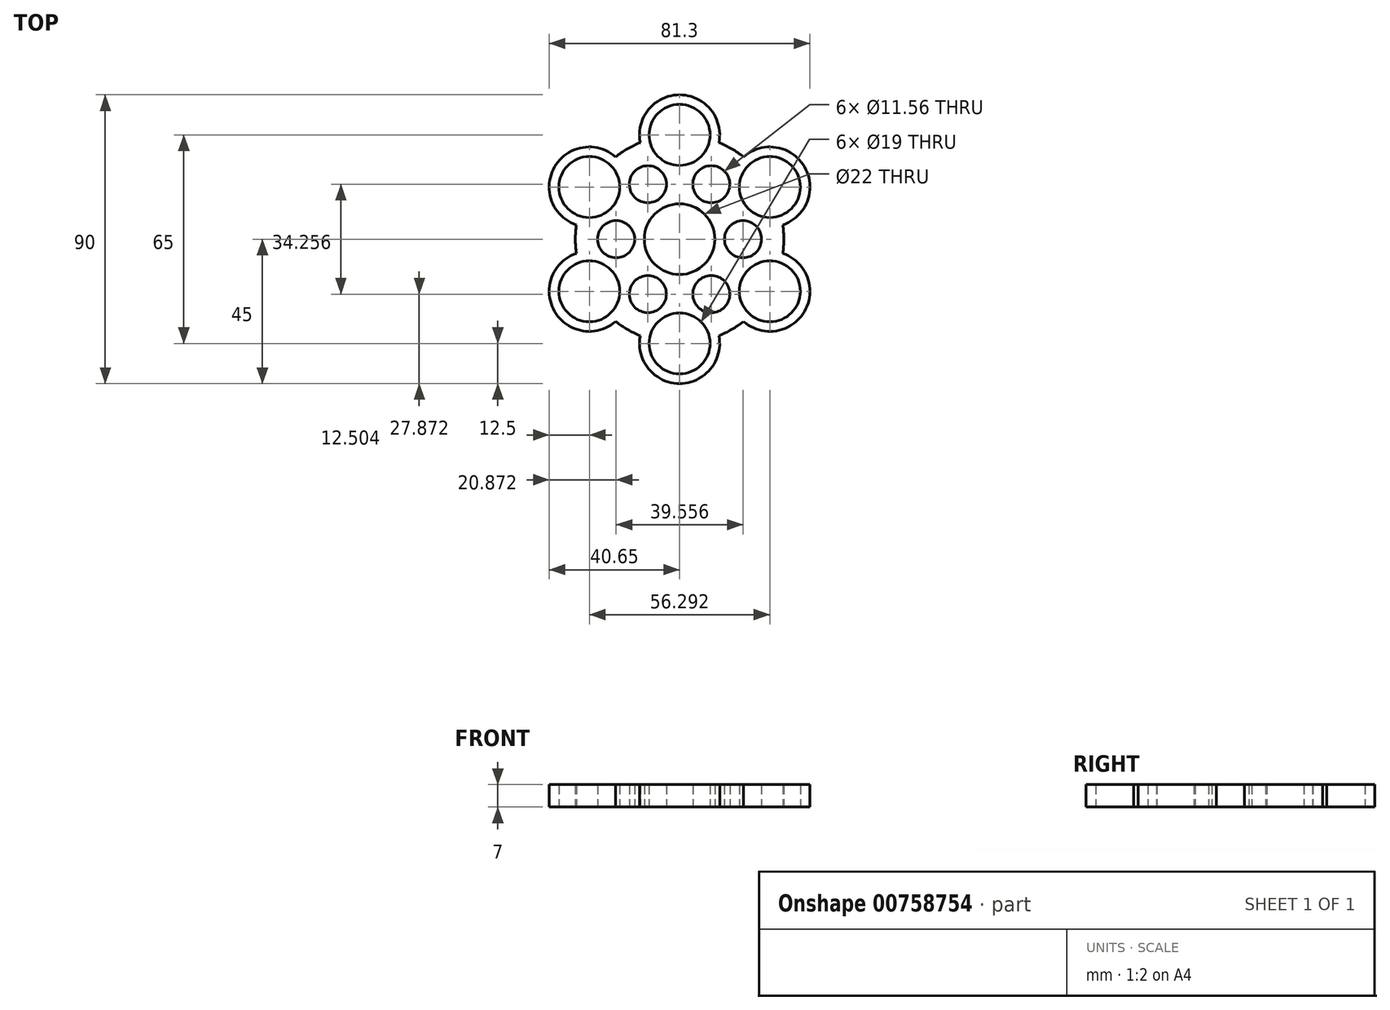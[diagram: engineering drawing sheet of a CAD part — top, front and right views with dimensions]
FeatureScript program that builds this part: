
annotation { "Feature Type Name" : "Feature", "Feature Type Description" : "" }
export const myFeature = defineFeature(function(context is Context, id is Id, definition is map)
    precondition{}
    {
        {
            var Q0;
            Q0=qCreatedBy(makeId("Top.planeOp"),FACE);
            var sketch = newSketch(context, id + "F0", { "sketchPlane" : qUnion([Q0])});
            skCircle(sketch, "E0", {"center": v(0, 0) * mm, "radius": 11 * mm});
            skCircle(sketch, "E1", {"center": v(0, 0) * mm, "radius": 14 * mm});
            skCircle(sketch, "E2", {"center": v(0, 32.5) * mm, "radius": 9.5 * mm});
            skArc(sketch, "E3.trimOffspring", {"start": v(12.27, 30.1) * mm, "mid": v(0, 45) * mm, "end": v(-12.27, 30.1) * mm});
            skCircle(sketch, "E4", {"center": v(0, 32.5) * mm, "radius": 12.5 * mm});
            skArc(sketch, "E5", {"start": v(-28.71, 6.77) * mm, "mid": v(-29.5, 0) * mm, "end": v(-28.71, -6.77) * mm});
            skArc(sketch, "E6", {"start": v(-31.64, 7.42) * mm, "mid": v(-32.5, 0) * mm, "end": v(-31.64, -7.42) * mm});
            skCircle(sketch, "E7.1.0", {"center": v(-28.15, 16.25) * mm, "radius": 12.5 * mm});
            skCircle(sketch, "E7.1.1", {"center": v(-28.15, 16.25) * mm, "radius": 9.5 * mm});
            skCircle(sketch, "E7.2.0", {"center": v(-28.15, -16.25) * mm, "radius": 12.5 * mm});
            skCircle(sketch, "E7.2.1", {"center": v(-28.15, -16.25) * mm, "radius": 9.5 * mm});
            skCircle(sketch, "E8.1.3.0", {"center": v(0, -32.5) * mm, "radius": 12.5 * mm});
            skCircle(sketch, "E8.2.3.0", {"center": v(0, -32.5) * mm, "radius": 9.5 * mm});
            skCircle(sketch, "E8.1.4.0", {"center": v(28.15, -16.25) * mm, "radius": 12.5 * mm});
            skCircle(sketch, "E8.2.4.0", {"center": v(28.15, -16.25) * mm, "radius": 9.5 * mm});
            skCircle(sketch, "E8.1.5.0", {"center": v(28.15, 16.25) * mm, "radius": 12.5 * mm});
            skCircle(sketch, "E8.2.5.0", {"center": v(28.15, 16.25) * mm, "radius": 9.5 * mm});
            skArc(sketch, "E9.trimOffspring", {"start": v(-9.4, 31.11) * mm, "mid": v(-16.25, 28.15) * mm, "end": v(-22.24, 23.7) * mm});
            skArc(sketch, "E10.trimOffspring", {"start": v(-8.5, 28.25) * mm, "mid": v(-14.75, 25.55) * mm, "end": v(-20.22, 21.48) * mm});
            skArc(sketch, "E11.trimOffspring", {"start": v(20.22, 21.48) * mm, "mid": v(14.75, 25.55) * mm, "end": v(8.5, 28.25) * mm});
            skArc(sketch, "E12.trimOffspring", {"start": v(22.24, 23.7) * mm, "mid": v(16.25, 28.15) * mm, "end": v(9.4, 31.11) * mm});
            skArc(sketch, "E13.trimOffspring", {"start": v(31.64, -7.42) * mm, "mid": v(32.5, 0) * mm, "end": v(31.64, 7.42) * mm});
            skArc(sketch, "E14.trimOffspring", {"start": v(28.71, -6.77) * mm, "mid": v(29.5, 0) * mm, "end": v(28.71, 6.77) * mm});
            skArc(sketch, "E15.trimOffspring", {"start": v(9.4, -31.11) * mm, "mid": v(16.25, -28.15) * mm, "end": v(22.24, -23.7) * mm});
            skArc(sketch, "E16.trimOffspring", {"start": v(8.5, -28.25) * mm, "mid": v(14.75, -25.55) * mm, "end": v(20.22, -21.48) * mm});
            skArc(sketch, "E17.trimOffspring", {"start": v(-22.24, -23.7) * mm, "mid": v(-16.25, -28.15) * mm, "end": v(-9.4, -31.11) * mm});
            skArc(sketch, "E18.trimOffspring", {"start": v(-20.22, -21.48) * mm, "mid": v(-14.75, -25.55) * mm, "end": v(-8.5, -28.25) * mm});
            skCircle(sketch, "E19", {"center": v(-9.89, 17.12) * mm, "radius": 5.78 * mm});
            skPoint(sketch, "E19.first.point", {"position": v(-15.66, 16.85) * mm});
            skPoint(sketch, "E19.second.point", {"position": v(-6.76, 21.99) * mm});
            skPoint(sketch, "E19.third.point", {"position": v(-6.76, 12.26) * mm});
            skCircle(sketch, "E20", {"center": v(9.89, 17.13) * mm, "radius": 5.78 * mm});
            skPoint(sketch, "E20.first.point", {"position": v(6.76, 21.99) * mm});
            skPoint(sketch, "E20.second.point", {"position": v(7, 12.12) * mm});
            skPoint(sketch, "E20.third.point", {"position": v(15.66, 16.85) * mm});
            skCircle(sketch, "E21", {"center": v(19.78, 0) * mm, "radius": 5.78 * mm});
            skPoint(sketch, "E21.first.point", {"position": v(22.42, -5.14) * mm});
            skPoint(sketch, "E21.second.point", {"position": v(22.42, 5.14) * mm});
            skPoint(sketch, "E21.third.point", {"position": v(14, 0) * mm});
            skCircle(sketch, "E22", {"center": v(9.89, -17.13) * mm, "radius": 5.78 * mm});
            skPoint(sketch, "E22.first.point", {"position": v(6.76, -21.99) * mm});
            skPoint(sketch, "E22.second.point", {"position": v(15.66, -16.85) * mm});
            skPoint(sketch, "E22.third.point", {"position": v(7, -12.12) * mm});
            skCircle(sketch, "E23", {"center": v(-9.89, -17.13) * mm, "radius": 5.78 * mm});
            skPoint(sketch, "E23.first.point", {"position": v(-6.76, -21.99) * mm});
            skPoint(sketch, "E23.second.point", {"position": v(-15.66, -16.85) * mm});
            skPoint(sketch, "E23.third.point", {"position": v(-7, -12.12) * mm});
            skCircle(sketch, "E24", {"center": v(-19.78, 0) * mm, "radius": 5.78 * mm});
            skPoint(sketch, "E24.first.point", {"position": v(-22.42, -5.14) * mm});
            skPoint(sketch, "E24.second.point", {"position": v(-22.42, 5.14) * mm});
            skPoint(sketch, "E24.third.point", {"position": v(-14, 0) * mm});
            skSolve(sketch);
        }
        {
            var Q0;
            {var subQ0=sQuery(id+"F0.wireOp",EDGE,"E11.trimOffspring");var subQ1=sQuery(id+"F0.wireOp",EDGE,"E2");var subQ2=makeQuery(id+"F0.imprint","INTERSECT",VERTEX,{"derivedFrom":[subQ1,subQ0]});Q0=makeQuery(id+"F0.imprint","IMPRINT",FACE,{"disambiguationData":[TD([[makeQuery(id+"F0.imprint","IMPRINT",EDGE,{"disambiguationData":[TD([[subQ2,-1.0]])],"derivedFrom":subQ1}),-1.0]])]});}
            var Q1;
            {var subQ0=sQuery(id+"F0.wireOp",EDGE,"E7.2.1");var subQ1=sQuery(id+"F0.wireOp",EDGE,"E5");var subQ2=makeQuery(id+"F0.imprint","INTERSECT",VERTEX,{"derivedFrom":[subQ1,subQ0]});Q1=makeQuery(id+"F0.imprint","IMPRINT",FACE,{"disambiguationData":[TD([[makeQuery(id+"F0.imprint","IMPRINT",EDGE,{"disambiguationData":[TD([[subQ2,1.0]])],"derivedFrom":subQ1}),-1.0]])]});}
            var Q2;
            {var subQ0=sQuery(id+"F0.wireOp",EDGE,"E15.trimOffspring");var subQ1=sQuery(id+"F0.wireOp",EDGE,"E8.1.4.0");var subQ2=makeQuery(id+"F0.imprint","INTERSECT",VERTEX,{"derivedFrom":[subQ1,subQ0]});Q2=makeQuery(id+"F0.imprint","IMPRINT",FACE,{"disambiguationData":[TD([[makeQuery(id+"F0.imprint","IMPRINT",EDGE,{"disambiguationData":[TD([[subQ2,1.0]])],"derivedFrom":subQ1}),1.0]])]});}
            var Q3;
            {var subQ0=sQuery(id+"F0.wireOp",EDGE,"E11.trimOffspring");var subQ1=sQuery(id+"F0.wireOp",EDGE,"E8.1.5.0");var subQ2=makeQuery(id+"F0.imprint","INTERSECT",VERTEX,{"derivedFrom":[subQ1,subQ0]});Q3=makeQuery(id+"F0.imprint","IMPRINT",FACE,{"disambiguationData":[TD([[makeQuery(id+"F0.imprint","IMPRINT",EDGE,{"disambiguationData":[TD([[subQ2,-1.0]])],"derivedFrom":subQ1}),1.0]])]});}
            var Q4;
            {var subQ0=sQuery(id+"F0.wireOp",EDGE,"E7.1.1");var subQ1=sQuery(id+"F0.wireOp",EDGE,"E5");var subQ2=makeQuery(id+"F0.imprint","INTERSECT",VERTEX,{"derivedFrom":[subQ1,subQ0]});Q4=makeQuery(id+"F0.imprint","IMPRINT",FACE,{"disambiguationData":[TD([[makeQuery(id+"F0.imprint","IMPRINT",EDGE,{"disambiguationData":[TD([[subQ2,-1.0]])],"derivedFrom":subQ1}),1.0]])]});}
            var Q5;
            {var subQ0=sQuery(id+"F0.wireOp",EDGE,"E17.trimOffspring");var subQ1=sQuery(id+"F0.wireOp",EDGE,"E7.2.0");var subQ2=makeQuery(id+"F0.imprint","INTERSECT",VERTEX,{"derivedFrom":[subQ1,subQ0]});Q5=makeQuery(id+"F0.imprint","IMPRINT",FACE,{"disambiguationData":[TD([[makeQuery(id+"F0.imprint","IMPRINT",EDGE,{"disambiguationData":[TD([[subQ2,-1.0]])],"derivedFrom":subQ1}),1.0]])]});}
            var Q6;
            {var subQ0=sQuery(id+"F0.wireOp",EDGE,"E13.trimOffspring");var subQ1=sQuery(id+"F0.wireOp",EDGE,"E8.1.5.0");var subQ2=makeQuery(id+"F0.imprint","INTERSECT",VERTEX,{"derivedFrom":[subQ1,subQ0]});Q6=makeQuery(id+"F0.imprint","IMPRINT",FACE,{"disambiguationData":[TD([[makeQuery(id+"F0.imprint","IMPRINT",EDGE,{"disambiguationData":[TD([[subQ2,1.0]])],"derivedFrom":subQ1}),1.0]])]});}
            var Q7;
            {var subQ0=sQuery(id+"F0.wireOp",EDGE,"E9.trimOffspring");var subQ1=sQuery(id+"F0.wireOp",EDGE,"E2");var subQ2=makeQuery(id+"F0.imprint","INTERSECT",VERTEX,{"derivedFrom":[subQ1,subQ0]});Q7=makeQuery(id+"F0.imprint","IMPRINT",FACE,{"disambiguationData":[TD([[makeQuery(id+"F0.imprint","IMPRINT",EDGE,{"disambiguationData":[TD([[subQ2,1.0]])],"derivedFrom":subQ1}),-1.0]])]});}
            var Q8;
            {var subQ0=sQuery(id+"F0.wireOp",EDGE,"E10.trimOffspring");var subQ1=sQuery(id+"F0.wireOp",EDGE,"E2");var subQ2=makeQuery(id+"F0.imprint","INTERSECT",VERTEX,{"derivedFrom":[subQ1,subQ0]});Q8=makeQuery(id+"F0.imprint","IMPRINT",FACE,{"disambiguationData":[TD([[makeQuery(id+"F0.imprint","IMPRINT",EDGE,{"disambiguationData":[TD([[subQ2,-1.0]])],"derivedFrom":subQ1}),-1.0]])]});}
            var Q9;
            {var subQ0=sQuery(id+"F0.wireOp",EDGE,"E15.trimOffspring");var subQ1=sQuery(id+"F0.wireOp",EDGE,"E8.1.3.0");var subQ2=makeQuery(id+"F0.imprint","INTERSECT",VERTEX,{"derivedFrom":[subQ1,subQ0]});Q9=makeQuery(id+"F0.imprint","IMPRINT",FACE,{"disambiguationData":[TD([[makeQuery(id+"F0.imprint","IMPRINT",EDGE,{"disambiguationData":[TD([[subQ2,-1.0]])],"derivedFrom":subQ1}),-1.0]])]});}
            var Q10;
            {var subQ0=sQuery(id+"F0.wireOp",EDGE,"E7.2.1");var subQ1=sQuery(id+"F0.wireOp",EDGE,"E5");var subQ2=makeQuery(id+"F0.imprint","INTERSECT",VERTEX,{"derivedFrom":[subQ1,subQ0]});Q10=makeQuery(id+"F0.imprint","IMPRINT",FACE,{"disambiguationData":[TD([[makeQuery(id+"F0.imprint","IMPRINT",EDGE,{"disambiguationData":[TD([[subQ2,1.0]])],"derivedFrom":subQ1}),1.0]])]});}
            var Q11;
            {var subQ0=sQuery(id+"F0.wireOp",EDGE,"E12.trimOffspring");var subQ1=sQuery(id+"F0.wireOp",EDGE,"E8.1.5.0");var subQ2=makeQuery(id+"F0.imprint","INTERSECT",VERTEX,{"derivedFrom":[subQ1,subQ0]});Q11=makeQuery(id+"F0.imprint","IMPRINT",FACE,{"disambiguationData":[TD([[makeQuery(id+"F0.imprint","IMPRINT",EDGE,{"disambiguationData":[TD([[subQ2,1.0]])],"derivedFrom":subQ1}),1.0]])]});}
            var Q12;
            {var subQ0=sQuery(id+"F0.wireOp",EDGE,"E12.trimOffspring");var subQ1=sQuery(id+"F0.wireOp",EDGE,"E4");var subQ2=makeQuery(id+"F0.imprint","INTERSECT",VERTEX,{"derivedFrom":[subQ1,subQ0]});Q12=makeQuery(id+"F0.imprint","IMPRINT",FACE,{"disambiguationData":[TD([[makeQuery(id+"F0.imprint","IMPRINT",EDGE,{"disambiguationData":[TD([[subQ2,1.0]])],"derivedFrom":subQ1}),-1.0]])]});}
            var Q13;
            {var subQ0=sQuery(id+"F0.wireOp",EDGE,"E13.trimOffspring");var subQ1=sQuery(id+"F0.wireOp",EDGE,"E8.1.4.0");var subQ2=makeQuery(id+"F0.imprint","INTERSECT",VERTEX,{"derivedFrom":[subQ1,subQ0]});Q13=makeQuery(id+"F0.imprint","IMPRINT",FACE,{"disambiguationData":[TD([[makeQuery(id+"F0.imprint","IMPRINT",EDGE,{"disambiguationData":[TD([[subQ2,-1.0]])],"derivedFrom":subQ1}),1.0]])]});}
            var Q14;
            {var subQ0=sQuery(id+"F0.wireOp",EDGE,"E9.trimOffspring");var subQ1=sQuery(id+"F0.wireOp",EDGE,"E7.1.0");var subQ2=makeQuery(id+"F0.imprint","INTERSECT",VERTEX,{"derivedFrom":[subQ1,subQ0]});Q14=makeQuery(id+"F0.imprint","IMPRINT",FACE,{"disambiguationData":[TD([[makeQuery(id+"F0.imprint","IMPRINT",EDGE,{"disambiguationData":[TD([[subQ2,1.0]])],"derivedFrom":subQ1}),1.0]])]});}
            var Q15;
            {var subQ0=sQuery(id+"F0.wireOp",EDGE,"E12.trimOffspring");var subQ1=sQuery(id+"F0.wireOp",EDGE,"E8.1.5.0");var subQ2=makeQuery(id+"F0.imprint","INTERSECT",VERTEX,{"derivedFrom":[subQ1,subQ0]});Q15=makeQuery(id+"F0.imprint","IMPRINT",FACE,{"disambiguationData":[TD([[makeQuery(id+"F0.imprint","IMPRINT",EDGE,{"disambiguationData":[TD([[subQ2,-1.0]])],"derivedFrom":subQ1}),1.0]])]});}
            var Q16;
            {var subQ0=sQuery(id+"F0.wireOp",EDGE,"E13.trimOffspring");var subQ1=sQuery(id+"F0.wireOp",EDGE,"E8.1.4.0");var subQ2=makeQuery(id+"F0.imprint","INTERSECT",VERTEX,{"derivedFrom":[subQ1,subQ0]});Q16=makeQuery(id+"F0.imprint","IMPRINT",FACE,{"disambiguationData":[TD([[makeQuery(id+"F0.imprint","IMPRINT",EDGE,{"disambiguationData":[TD([[subQ2,1.0]])],"derivedFrom":subQ1}),1.0]])]});}
            var Q17;
            {var subQ0=sQuery(id+"F0.wireOp",EDGE,"E7.1.1");var subQ1=sQuery(id+"F0.wireOp",EDGE,"E6");var subQ2=makeQuery(id+"F0.imprint","INTERSECT",VERTEX,{"derivedFrom":[subQ1,subQ0]});Q17=makeQuery(id+"F0.imprint","IMPRINT",FACE,{"disambiguationData":[TD([[makeQuery(id+"F0.imprint","IMPRINT",EDGE,{"disambiguationData":[TD([[subQ2,-1.0]])],"derivedFrom":subQ1}),-1.0]])]});}
            var Q18;
            {var subQ0=sQuery(id+"F0.wireOp",EDGE,"E17.trimOffspring");var subQ1=sQuery(id+"F0.wireOp",EDGE,"E7.2.0");var subQ2=makeQuery(id+"F0.imprint","INTERSECT",VERTEX,{"derivedFrom":[subQ1,subQ0]});Q18=makeQuery(id+"F0.imprint","IMPRINT",FACE,{"disambiguationData":[TD([[makeQuery(id+"F0.imprint","IMPRINT",EDGE,{"disambiguationData":[TD([[subQ2,-1.0]])],"derivedFrom":subQ1}),-1.0]])]});}
            var Q19;
            {var subQ0=sQuery(id+"F0.wireOp",EDGE,"E17.trimOffspring");var subQ1=sQuery(id+"F0.wireOp",EDGE,"E8.1.3.0");var subQ2=makeQuery(id+"F0.imprint","INTERSECT",VERTEX,{"derivedFrom":[subQ1,subQ0]});Q19=makeQuery(id+"F0.imprint","IMPRINT",FACE,{"disambiguationData":[TD([[makeQuery(id+"F0.imprint","IMPRINT",EDGE,{"disambiguationData":[TD([[subQ2,1.0]])],"derivedFrom":subQ1}),1.0]])]});}
            var Q20;
            {var subQ0=sQuery(id+"F0.wireOp",EDGE,"E15.trimOffspring");var subQ1=sQuery(id+"F0.wireOp",EDGE,"E8.1.3.0");var subQ2=makeQuery(id+"F0.imprint","INTERSECT",VERTEX,{"derivedFrom":[subQ1,subQ0]});Q20=makeQuery(id+"F0.imprint","IMPRINT",FACE,{"disambiguationData":[TD([[makeQuery(id+"F0.imprint","IMPRINT",EDGE,{"disambiguationData":[TD([[subQ2,1.0]])],"derivedFrom":subQ1}),1.0]])]});}
            var Q21;
            {var subQ0=sQuery(id+"F0.wireOp",EDGE,"E9.trimOffspring");var subQ1=sQuery(id+"F0.wireOp",EDGE,"E4");var subQ2=makeQuery(id+"F0.imprint","INTERSECT",VERTEX,{"derivedFrom":[subQ1,subQ0]});Q21=makeQuery(id+"F0.imprint","IMPRINT",FACE,{"disambiguationData":[TD([[makeQuery(id+"F0.imprint","IMPRINT",EDGE,{"disambiguationData":[TD([[subQ2,-1.0]])],"derivedFrom":subQ1}),-1.0]])]});}
            var Q22;
            {var subQ0=sQuery(id+"F0.wireOp",EDGE,"E14.trimOffspring");var subQ1=sQuery(id+"F0.wireOp",EDGE,"E8.1.4.0");var subQ2=makeQuery(id+"F0.imprint","INTERSECT",VERTEX,{"derivedFrom":[subQ1,subQ0]});Q22=makeQuery(id+"F0.imprint","IMPRINT",FACE,{"disambiguationData":[TD([[makeQuery(id+"F0.imprint","IMPRINT",EDGE,{"disambiguationData":[TD([[subQ2,-1.0]])],"derivedFrom":subQ1}),1.0]])]});}
            var Q23;
            {var subQ0=sQuery(id+"F0.wireOp",EDGE,"E16.trimOffspring");var subQ1=sQuery(id+"F0.wireOp",EDGE,"E8.1.3.0");var subQ2=makeQuery(id+"F0.imprint","INTERSECT",VERTEX,{"derivedFrom":[subQ1,subQ0]});Q23=makeQuery(id+"F0.imprint","IMPRINT",FACE,{"disambiguationData":[TD([[makeQuery(id+"F0.imprint","IMPRINT",EDGE,{"disambiguationData":[TD([[subQ2,-1.0]])],"derivedFrom":subQ1}),1.0]])]});}
            var Q24;
            {var subQ0=sQuery(id+"F0.wireOp",EDGE,"E13.trimOffspring");var subQ1=sQuery(id+"F0.wireOp",EDGE,"E8.1.4.0");var subQ2=makeQuery(id+"F0.imprint","INTERSECT",VERTEX,{"derivedFrom":[subQ1,subQ0]});Q24=makeQuery(id+"F0.imprint","IMPRINT",FACE,{"disambiguationData":[TD([[makeQuery(id+"F0.imprint","IMPRINT",EDGE,{"disambiguationData":[TD([[subQ2,-1.0]])],"derivedFrom":subQ1}),-1.0]])]});}
            var Q25;
            {var subQ0=sQuery(id+"F0.wireOp",EDGE,"E7.1.0");var subQ1=sQuery(id+"F0.wireOp",EDGE,"E5");var subQ2=makeQuery(id+"F0.imprint","INTERSECT",VERTEX,{"derivedFrom":[subQ1,subQ0]});Q25=makeQuery(id+"F0.imprint","IMPRINT",FACE,{"disambiguationData":[TD([[makeQuery(id+"F0.imprint","IMPRINT",EDGE,{"disambiguationData":[TD([[subQ2,-1.0]])],"derivedFrom":subQ1}),-1.0]])]});}
            var Q26;
            {var subQ0=sQuery(id+"F0.wireOp",EDGE,"E7.1.1");var subQ1=sQuery(id+"F0.wireOp",EDGE,"E5");var subQ2=makeQuery(id+"F0.imprint","INTERSECT",VERTEX,{"derivedFrom":[subQ1,subQ0]});Q26=makeQuery(id+"F0.imprint","IMPRINT",FACE,{"disambiguationData":[TD([[makeQuery(id+"F0.imprint","IMPRINT",EDGE,{"disambiguationData":[TD([[subQ2,-1.0]])],"derivedFrom":subQ1}),-1.0]])]});}
            var Q27;
            {var subQ0=sQuery(id+"F0.wireOp",EDGE,"E15.trimOffspring");var subQ1=sQuery(id+"F0.wireOp",EDGE,"E8.1.3.0");var subQ2=makeQuery(id+"F0.imprint","INTERSECT",VERTEX,{"derivedFrom":[subQ1,subQ0]});Q27=makeQuery(id+"F0.imprint","IMPRINT",FACE,{"disambiguationData":[TD([[makeQuery(id+"F0.imprint","IMPRINT",EDGE,{"disambiguationData":[TD([[subQ2,-1.0]])],"derivedFrom":subQ1}),1.0]])]});}
            var Q28;
            {var subQ0=sQuery(id+"F0.wireOp",EDGE,"E7.2.1");var subQ1=sQuery(id+"F0.wireOp",EDGE,"E6");var subQ2=makeQuery(id+"F0.imprint","INTERSECT",VERTEX,{"derivedFrom":[subQ1,subQ0]});Q28=makeQuery(id+"F0.imprint","IMPRINT",FACE,{"disambiguationData":[TD([[makeQuery(id+"F0.imprint","IMPRINT",EDGE,{"disambiguationData":[TD([[subQ2,1.0]])],"derivedFrom":subQ1}),-1.0]])]});}
            var Q29;
            {var subQ0=sQuery(id+"F0.wireOp",EDGE,"E9.trimOffspring");var subQ1=sQuery(id+"F0.wireOp",EDGE,"E2");var subQ2=makeQuery(id+"F0.imprint","INTERSECT",VERTEX,{"derivedFrom":[subQ1,subQ0]});Q29=makeQuery(id+"F0.imprint","IMPRINT",FACE,{"disambiguationData":[TD([[makeQuery(id+"F0.imprint","IMPRINT",EDGE,{"disambiguationData":[TD([[subQ2,-1.0]])],"derivedFrom":subQ1}),-1.0]])]});}
            var Q30;
            Q30=makeQuery(id+"F0.imprint","IMPRINT",FACE,{"disambiguationData":[TD([[makeQuery(id+"F0.imprint","IMPRINT",EDGE,{"derivedFrom":sQuery(id+"F0.wireOp",EDGE,"E0")}),-1.0]])]});
            var Q31;
            {var subQ0=sQuery(id+"F0.wireOp",EDGE,"E24");var subQ1=sQuery(id+"F0.wireOp",EDGE,"E1");var subQ2=makeQuery(id+"F0.imprint","INTERSECT",VERTEX,{"disambiguationData":[OD(0.0)],"derivedFrom":[subQ1,subQ0]});Q31=makeQuery(id+"F0.imprint","IMPRINT",FACE,{"disambiguationData":[TD([[makeQuery(id+"F0.imprint","IMPRINT",EDGE,{"disambiguationData":[TD([[subQ2,1.0]])],"derivedFrom":subQ1}),-1.0]])]});}
            var Q32;
            {var subQ0=sQuery(id+"F0.wireOp",EDGE,"E7.1.0");var subQ1=sQuery(id+"F0.wireOp",EDGE,"E5");var subQ2=makeQuery(id+"F0.imprint","INTERSECT",VERTEX,{"derivedFrom":[subQ1,subQ0]});Q32=makeQuery(id+"F0.imprint","IMPRINT",FACE,{"disambiguationData":[TD([[makeQuery(id+"F0.imprint","IMPRINT",EDGE,{"disambiguationData":[TD([[subQ2,-1.0]])],"derivedFrom":subQ1}),1.0]])]});}
            var Q33;
            {var subQ0=sQuery(id+"F0.wireOp",EDGE,"E24");var subQ1=sQuery(id+"F0.wireOp",EDGE,"E1");var subQ2=makeQuery(id+"F0.imprint","INTERSECT",VERTEX,{"disambiguationData":[OD(1.0)],"derivedFrom":[subQ1,subQ0]});Q33=makeQuery(id+"F0.imprint","IMPRINT",FACE,{"disambiguationData":[TD([[makeQuery(id+"F0.imprint","IMPRINT",EDGE,{"disambiguationData":[TD([[subQ2,-1.0]])],"derivedFrom":subQ1}),-1.0]])]});}
            var Q34;
            {var subQ0=sQuery(id+"F0.wireOp",EDGE,"E19");var subQ1=sQuery(id+"F0.wireOp",EDGE,"E4");var subQ2=makeQuery(id+"F0.imprint","INTERSECT",VERTEX,{"disambiguationData":[OD(0.0)],"derivedFrom":[subQ1,subQ0]});Q34=makeQuery(id+"F0.imprint","IMPRINT",FACE,{"disambiguationData":[TD([[makeQuery(id+"F0.imprint","IMPRINT",EDGE,{"disambiguationData":[TD([[subQ2,1.0]])],"derivedFrom":subQ1}),-1.0]])]});}
            var Q35;
            {var subQ0=sQuery(id+"F0.wireOp",EDGE,"E20");var subQ1=sQuery(id+"F0.wireOp",EDGE,"E1");var subQ2=makeQuery(id+"F0.imprint","INTERSECT",VERTEX,{"disambiguationData":[OD(1.0)],"derivedFrom":[subQ1,subQ0]});Q35=makeQuery(id+"F0.imprint","IMPRINT",FACE,{"disambiguationData":[TD([[makeQuery(id+"F0.imprint","IMPRINT",EDGE,{"disambiguationData":[TD([[subQ2,-1.0]])],"derivedFrom":subQ1}),-1.0]])]});}
            var Q36;
            {var subQ0=sQuery(id+"F0.wireOp",EDGE,"E21");var subQ1=sQuery(id+"F0.wireOp",EDGE,"E1");var subQ2=makeQuery(id+"F0.imprint","INTERSECT",VERTEX,{"disambiguationData":[OD(0.0)],"derivedFrom":[subQ1,subQ0]});Q36=makeQuery(id+"F0.imprint","IMPRINT",FACE,{"disambiguationData":[TD([[makeQuery(id+"F0.imprint","IMPRINT",EDGE,{"disambiguationData":[TD([[subQ2,-1.0]])],"derivedFrom":subQ1}),-1.0]])]});}
            var Q37;
            {var subQ0=sQuery(id+"F0.wireOp",EDGE,"E20");var subQ1=sQuery(id+"F0.wireOp",EDGE,"E4");var subQ2=makeQuery(id+"F0.imprint","INTERSECT",VERTEX,{"disambiguationData":[OD(1.0)],"derivedFrom":[subQ1,subQ0]});Q37=makeQuery(id+"F0.imprint","IMPRINT",FACE,{"disambiguationData":[TD([[makeQuery(id+"F0.imprint","IMPRINT",EDGE,{"disambiguationData":[TD([[subQ2,-1.0]])],"derivedFrom":subQ1}),-1.0]])]});}
            var Q38;
            {var subQ0=sQuery(id+"F0.wireOp",EDGE,"E14.trimOffspring");var subQ1=sQuery(id+"F0.wireOp",EDGE,"E8.1.4.0");var subQ2=makeQuery(id+"F0.imprint","INTERSECT",VERTEX,{"derivedFrom":[subQ1,subQ0]});Q38=makeQuery(id+"F0.imprint","IMPRINT",FACE,{"disambiguationData":[TD([[makeQuery(id+"F0.imprint","IMPRINT",EDGE,{"disambiguationData":[TD([[subQ2,-1.0]])],"derivedFrom":subQ1}),-1.0]])]});}
            var Q39;
            {var subQ0=sQuery(id+"F0.wireOp",EDGE,"E21");var subQ1=sQuery(id+"F0.wireOp",EDGE,"E1");var subQ2=makeQuery(id+"F0.imprint","INTERSECT",VERTEX,{"disambiguationData":[OD(1.0)],"derivedFrom":[subQ1,subQ0]});Q39=makeQuery(id+"F0.imprint","IMPRINT",FACE,{"disambiguationData":[TD([[makeQuery(id+"F0.imprint","IMPRINT",EDGE,{"disambiguationData":[TD([[subQ2,1.0]])],"derivedFrom":subQ1}),-1.0]])]});}
            var Q40;
            {var subQ0=sQuery(id+"F0.wireOp",EDGE,"E16.trimOffspring");var subQ1=sQuery(id+"F0.wireOp",EDGE,"E8.1.3.0");var subQ2=makeQuery(id+"F0.imprint","INTERSECT",VERTEX,{"derivedFrom":[subQ1,subQ0]});Q40=makeQuery(id+"F0.imprint","IMPRINT",FACE,{"disambiguationData":[TD([[makeQuery(id+"F0.imprint","IMPRINT",EDGE,{"disambiguationData":[TD([[subQ2,-1.0]])],"derivedFrom":subQ1}),-1.0]])]});}
            var Q41;
            {var subQ0=sQuery(id+"F0.wireOp",EDGE,"E23");var subQ1=sQuery(id+"F0.wireOp",EDGE,"E1");var subQ2=makeQuery(id+"F0.imprint","INTERSECT",VERTEX,{"disambiguationData":[OD(1.0)],"derivedFrom":[subQ1,subQ0]});Q41=makeQuery(id+"F0.imprint","IMPRINT",FACE,{"disambiguationData":[TD([[makeQuery(id+"F0.imprint","IMPRINT",EDGE,{"disambiguationData":[TD([[subQ2,-1.0]])],"derivedFrom":subQ1}),-1.0]])]});}
            var Q42;
            {var subQ0=sQuery(id+"F0.wireOp",EDGE,"E18.trimOffspring");var subQ1=sQuery(id+"F0.wireOp",EDGE,"E7.2.0");var subQ2=makeQuery(id+"F0.imprint","INTERSECT",VERTEX,{"derivedFrom":[subQ1,subQ0]});Q42=makeQuery(id+"F0.imprint","IMPRINT",FACE,{"disambiguationData":[TD([[makeQuery(id+"F0.imprint","IMPRINT",EDGE,{"disambiguationData":[TD([[subQ2,-1.0]])],"derivedFrom":subQ1}),-1.0]])]});}
            extrude(context, id + "F1", {"entities" : qUnion([Q0, Q1, Q2, Q3, Q4, Q5, Q6, Q7, Q8, Q9, Q10, Q11, Q12, Q13, Q14, Q15, Q16, Q17, Q18, Q19, Q20, Q21, Q22, Q23, Q24, Q25, Q26, Q27, Q28, Q29, Q30, Q31, Q32, Q33, Q34, Q35, Q36, Q37, Q38, Q39, Q40, Q41, Q42]), "depth" : 7 * mm, "offsetDistance" : 25 * mm});
        }
    });
